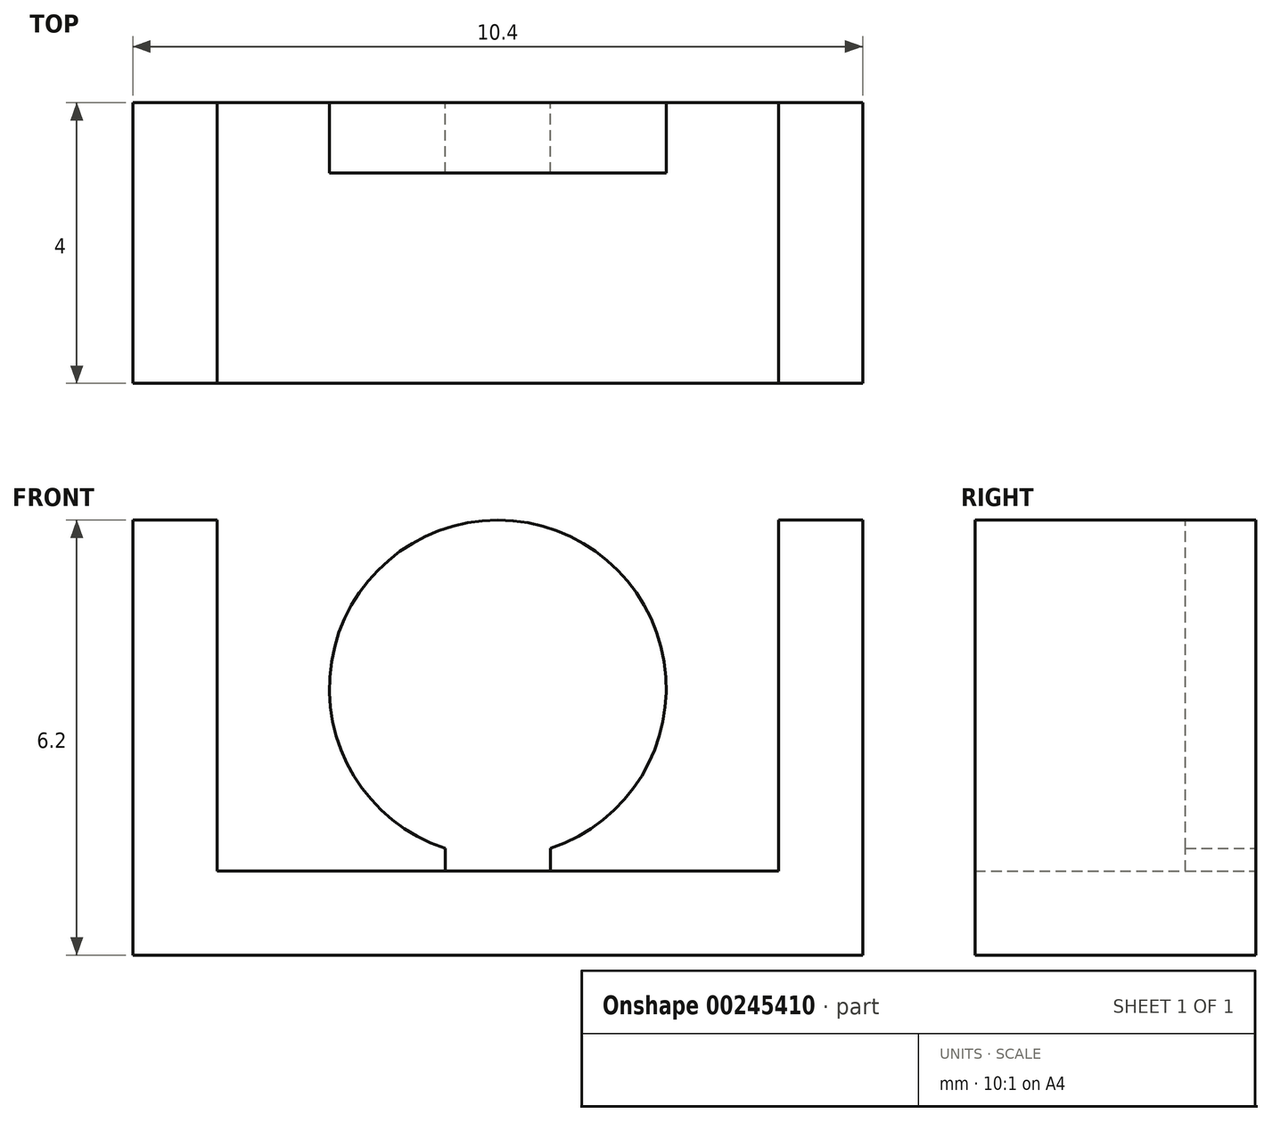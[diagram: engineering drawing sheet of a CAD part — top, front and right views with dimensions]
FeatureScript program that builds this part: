
annotation { "Feature Type Name" : "Feature", "Feature Type Description" : "" }
export const myFeature = defineFeature(function(context is Context, id is Id, definition is map)
    precondition{}
    {
        {
            var Q0;
            Q0=qCreatedBy(makeId("Front.planeOp"),FACE);
            var sketch = newSketch(context, id + "F0", { "sketchPlane" : qUnion([Q0])});
            skLineSegment(sketch, "E0", {"start": v(0, 0) * mm, "end": v(0, 5) * mm});
            skLineSegment(sketch, "E1", {"start": v(0, 5) * mm, "end": v(1.2, 5) * mm});
            skLineSegment(sketch, "E2", {"start": v(1.2, 5) * mm, "end": v(1.2, 0) * mm});
            skLineSegment(sketch, "E3", {"start": v(1.2, 0) * mm, "end": v(9.2, 0) * mm});
            skLineSegment(sketch, "E4", {"start": v(9.2, 0) * mm, "end": v(9.2, 5) * mm});
            skLineSegment(sketch, "E5", {"start": v(9.2, 5) * mm, "end": v(10.4, 5) * mm});
            skLineSegment(sketch, "E6", {"start": v(10.4, 5) * mm, "end": v(10.4, 0) * mm});
            skLineSegment(sketch, "E7", {"start": v(10.4, 0) * mm, "end": v(10.4, -1.2) * mm});
            skLineSegment(sketch, "E8", {"start": v(10.4, -1.2) * mm, "end": v(0, -1.2) * mm});
            skLineSegment(sketch, "E9", {"start": v(0, -1.2) * mm, "end": v(0, 0) * mm});
            skSolve(sketch);
        }
        {
            var Q0;
            Q0=qSketchRegion(id+"F0",true);
            extrude(context, id + "F1", {"entities" : qUnion([Q0]), "depth" : 5 * mm});
        }
        {
            var Q0;
            Q0=makeQuery(id+"F1.opExtrude","SWEPT_FACE",FACE,{"disambiguationData":[OSD([sQuery(id+"F0.wireOp",EDGE,"E3")])]});
            var sketch = newSketch(context, id + "F2", { "sketchPlane" : qUnion([Q0])});
            skLineSegment(sketch, "E10", {"start": v(5.2, 0) * mm, "end": v(5.2, -5) * mm});
            skCircle(sketch, "E11", {"center": v(5.2, -2.5) * mm, "radius": 0.78 * mm});
            skSolve(sketch);
        }
        {
            var Q0;
            Q0=qSketchRegion(id+"F2",true);
            var Q1;
            Q1=sQuery(id+"F2.wireOp",EDGE,"E11");
            extrude(context, id + "F3", {"entities" : qUnion([Q0]), "operationType" : NewBodyOperationType.ADD, "surfaceEntities" : qUnion([Q1]), "depth" : 1.9 * mm, "hasDraft" : true, "draftAngle" : 10 * degree, "draftPullDirection" : true});
        }
        {
            var Q0;
            Q0=makeQuery(id+"F1.opExtrude","CAP_FACE",FACE,{"disambiguationData":[OSD([sQuery(id+"F0.wireOp",EDGE,"E0"),sQuery(id+"F0.wireOp",EDGE,"E1"),sQuery(id+"F0.wireOp",EDGE,"E2"),sQuery(id+"F0.wireOp",EDGE,"E3"),sQuery(id+"F0.wireOp",EDGE,"E4"),sQuery(id+"F0.wireOp",EDGE,"E5"),sQuery(id+"F0.wireOp",EDGE,"E6"),sQuery(id+"F0.wireOp",EDGE,"E7"),sQuery(id+"F0.wireOp",EDGE,"E8"),sQuery(id+"F0.wireOp",EDGE,"E9")])],"isStart":true});
            var sketch = newSketch(context, id + "F4", { "sketchPlane" : qUnion([Q0])});
            skLineSegment(sketch, "E12", {"start": v(-5.2, 5) * mm, "end": v(-5.2, 2.6) * mm});
            skCircle(sketch, "E13", {"center": v(-5.2, 2.6) * mm, "radius": 2.4 * mm});
            skLineSegment(sketch, "E14.bottom", {"start": v(-4.45, 0) * mm, "end": v(-5.95, 0) * mm});
            skLineSegment(sketch, "E14.left", {"start": v(-4.45, 0) * mm, "end": v(-4.45, 0.32) * mm});
            skLineSegment(sketch, "E14.right", {"start": v(-5.95, 0) * mm, "end": v(-5.95, 0.32) * mm});
            skPoint(sketch, "E14.top.end.orphan", {"position": v(-5.95, 5.2) * mm});
            skPoint(sketch, "E15.trimOffspring.end.orphan", {"position": v(-4.45, 5.2) * mm});
            skPoint(sketch, "E16.orphan", {"position": v(-1.2, 5) * mm});
            skPoint(sketch, "E17.start.orphan", {"position": v(-9.2, 5) * mm});
            skSolve(sketch);
        }
        {
            var Q0;
            Q0=qSketchRegion(id+"F4",true);
            extrude(context, id + "F5", {"entities" : qUnion([Q0]), "operationType" : NewBodyOperationType.ADD, "oppositeDirection" : true, "depth" : 1 * mm});
        }
        {
            var Q0;
            Q0=makeQuery(id+"F1.opExtrude","SWEPT_FACE",FACE,{"disambiguationData":[OSD([sQuery(id+"F0.wireOp",EDGE,"E3")])]});
            var sketch = newSketch(context, id + "F6", { "sketchPlane" : qUnion([Q0])});
            skLineSegment(sketch, "E18.bottom", {"start": v(1.2, -5) * mm, "end": v(9.2, -5) * mm});
            skLineSegment(sketch, "E18.top", {"start": v(1.2, -1.54) * mm, "end": v(9.2, -1.54) * mm});
            skLineSegment(sketch, "E18.left", {"start": v(1.2, -5) * mm, "end": v(1.2, -1.54) * mm});
            skLineSegment(sketch, "E18.right", {"start": v(9.2, -5) * mm, "end": v(9.2, -1.54) * mm});
            skSolve(sketch);
        }
        {
            var Q0;
            Q0=qSketchRegion(id+"F6",true);
            extrude(context, id + "F7", {"entities" : qUnion([Q0]), "operationType" : NewBodyOperationType.REMOVE, "depth" : 25 * mm});
        }
        {
            var Q0;
            Q0=makeQuery(id+"F1.opExtrude","SWEPT_FACE",FACE,{"disambiguationData":[OSD([sQuery(id+"F0.wireOp",EDGE,"E5")])]});
            var sketch = newSketch(context, id + "F8", { "sketchPlane" : qUnion([Q0])});
            skLineSegment(sketch, "E19.bottom", {"start": v(10.4, -5) * mm, "end": v(-4.08, -5) * mm});
            skLineSegment(sketch, "E19.top", {"start": v(10.4, -4) * mm, "end": v(-4.08, -4) * mm});
            skLineSegment(sketch, "E19.left", {"start": v(10.4, -5) * mm, "end": v(10.4, -4) * mm});
            skLineSegment(sketch, "E19.right", {"start": v(-4.08, -5) * mm, "end": v(-4.08, -4) * mm});
            skSolve(sketch);
        }
        {
            var Q0;
            Q0=qSketchRegion(id+"F8",true);
            extrude(context, id + "F9", {"entities" : qUnion([Q0]), "operationType" : NewBodyOperationType.REMOVE, "oppositeDirection" : true, "depth" : 25 * mm});
        }
    });
